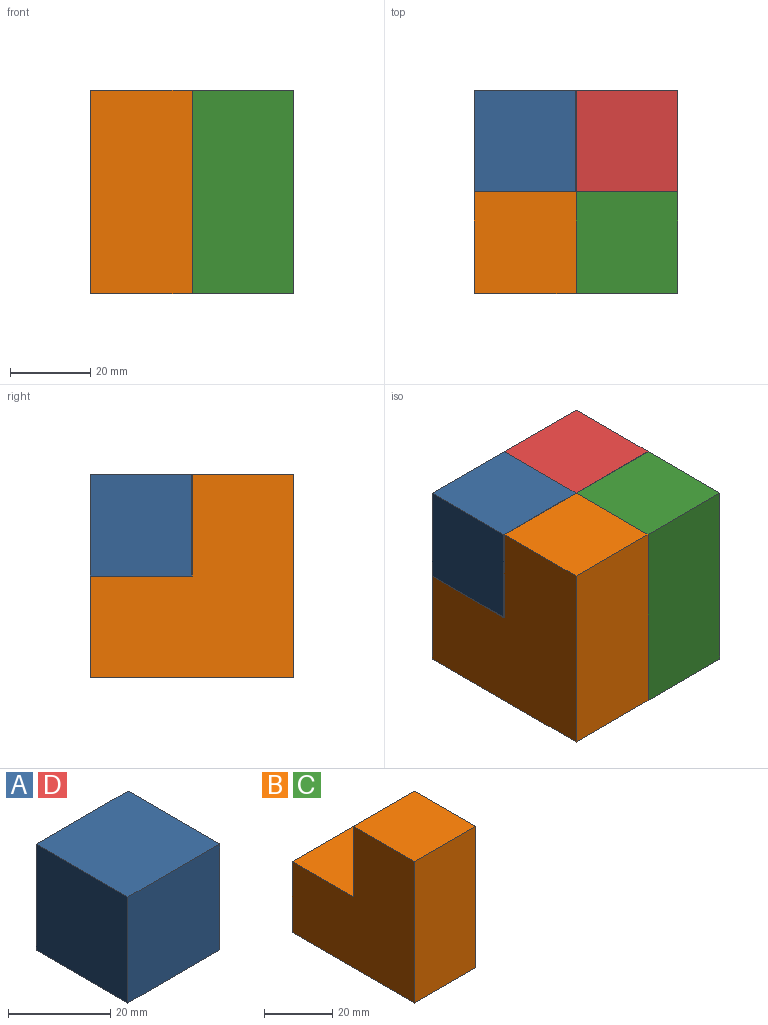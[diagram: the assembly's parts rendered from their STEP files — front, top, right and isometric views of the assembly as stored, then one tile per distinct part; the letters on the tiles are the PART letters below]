
ASSEMBLY  parts=4 mates=3
PART A: 6 faces, bbox 25.5x25.4x25.4 mm
  f0: plane 25.4x25.4mm, normal (1,0,0), area 645.2mm2, adj f1,f3,f4,f5
  f1: plane 25.46x25.4mm, normal (0,0,1), area 646.7mm2, adj f0,f2,f4,f5
  f2: plane 25.4x25.4mm, normal (-1,0,0), area 645.2mm2, adj f1,f3,f4,f5
  f3: plane 25.46x25.4mm, normal (0,0,-1), area 646.7mm2, adj f0,f2,f4,f5
  f4: plane 25.46x25.4mm, normal (0,-1,0), area 646.7mm2, adj f0,f1,f2,f3
  f5: plane 25.46x25.4mm, normal (0,1,0), area 646.7mm2, adj f0,f1,f2,f3
PART B: 8 faces, bbox 25.4x50.8x50.8 mm
  f0: plane 25.4x25.4mm, normal (0,0,1), area 645.2mm2, adj f1,f5,f6,f7
  f1: plane 25.4x25.4mm, normal (0,1,0), area 645.2mm2, adj f0,f2,f6,f7
  f2: plane 25.4x25.4mm, normal (0,0,1), area 645.2mm2, adj f1,f3,f6,f7
  f3: plane 50.8x25.4mm, normal (0,-1,0), area 1290.3mm2, adj f2,f4,f6,f7
  f4: plane 50.8x25.4mm, normal (0,0,-1), area 1290.3mm2, adj f3,f5,f6,f7
  f5: plane 25.4x25.4mm, normal (0,1,0), area 645.2mm2, adj f0,f4,f6,f7
  f6: plane 50.8x50.8mm, normal (1,0,0), area 1935.5mm2, adj f0,f1,f2,f3,f4,f5
  f7: plane 50.8x50.8mm, normal (-1,0,0), area 1935.5mm2, adj f0,f1,f2,f3,f4,f5
PART C: same geometry as B
PART D: same geometry as A
PLACE A t=(56.71,55.51,-1.15)mm
PLACE B t=(31.34,4.71,24.25)mm
PLACE C t=(56.74,4.71,24.25)mm
PLACE D t=(82.17,55.51,-1.15)mm
MATE fastened A.f0 <-> D.f2  axis (1,0,0) through (56.71,42.81,11.55)mm
MATE fastened B.f6 <-> C.f7  axis (1,0,0) through (56.74,25.87,-5.38)mm
MATE fastened C.f0 <-> D.f3  axis (0,0,1) through (69.44,42.81,-1.15)mm
